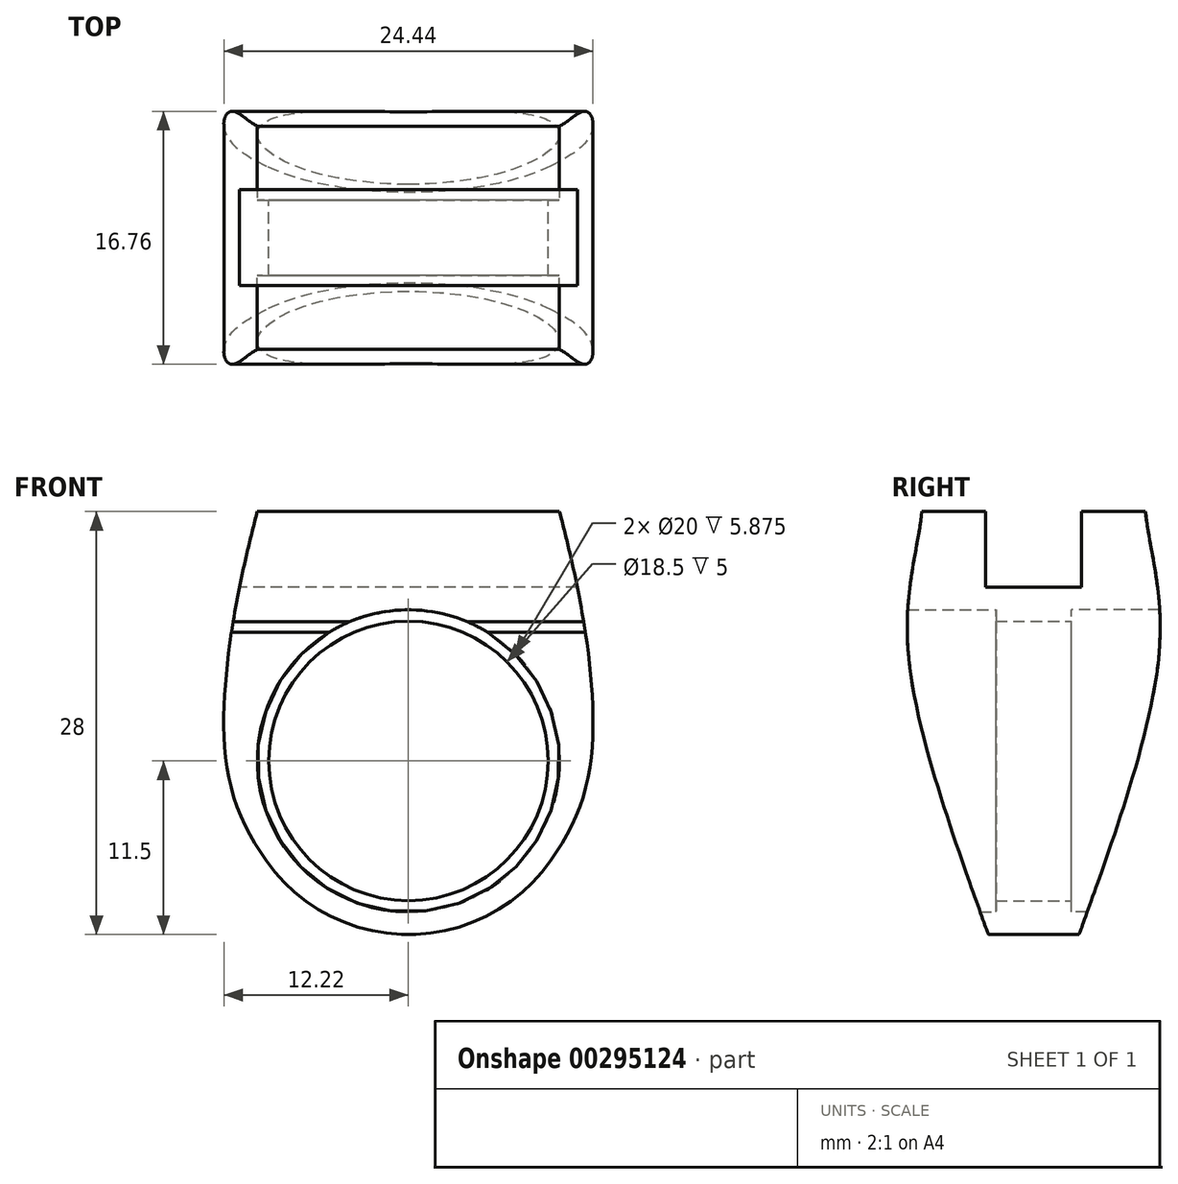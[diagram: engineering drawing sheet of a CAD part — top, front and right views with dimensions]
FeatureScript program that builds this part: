
annotation { "Feature Type Name" : "Feature", "Feature Type Description" : "" }
export const myFeature = defineFeature(function(context is Context, id is Id, definition is map)
    precondition{}
    {
        {
            var Q0;
            Q0=qCreatedBy(makeId("Front.planeOp"),FACE);
            var sketch = newSketch(context, id + "F0", { "sketchPlane" : qUnion([Q0])});
            skCircle(sketch, "E0", {"center": v(0, 0) * mm, "radius": 8.5 * mm});
            skCircle(sketch, "E1", {"center": v(0, 0) * mm, "radius": 11.5 * mm});
            skSolve(sketch);
        }
        {
            var Q0;
            Q0=qCreatedBy(makeId("Front.planeOp"),FACE);
            var sketch = newSketch(context, id + "F1", { "sketchPlane" : qUnion([Q0])});
            skLineSegment(sketch, "E2", {"start": v(-10, 16.5) * mm, "end": v(10, 16.5) * mm});
            skLineSegment(sketch, "E3", {"start": v(-8.5, 0) * mm, "end": v(-11.5, 0) * mm, "construction": true});
            skLineSegment(sketch, "E4", {"start": v(-10, 16.5) * mm, "end": v(-10, 0) * mm, "construction": true});
            skLineSegment(sketch, "E5", {"start": v(-10, 16.5) * mm, "end": v(-14.42, 0) * mm, "construction": true});
            skLineSegment(sketch, "E6", {"start": v(0, 0) * mm, "end": v(-9.42, -6.6) * mm, "construction": true});
            skFitSpline(sketch, "E7", {"points": [v(-9.42, -6.6) * mm, v(-12.07, 0) * mm, v(-10, 16.5) * mm], "startDerivative": vector(-9.97, 14.24) * mm, "endDerivative": vector(8.14, 30.38) * mm});
            skLineSegment(sketch, "E8", {"start": v(-9.42, -6.6) * mm, "end": v(-7.7, -9.05) * mm, "construction": true});
            skFitSpline(sketch, "E9.MirrorCS", {"points": [v(9.42, -6.6) * mm, v(12.07, 0) * mm, v(10, 16.5) * mm], "startDerivative": vector(9.97, 14.24) * mm, "endDerivative": vector(-8.14, 30.38) * mm});
            skCircle(sketch, "E10", {"center": v(0, 0) * mm, "radius": 8.5 * mm});
            skArc(sketch, "E11", {"start": v(-9.42, -6.6) * mm, "mid": v(0, -11.5) * mm, "end": v(9.42, -6.6) * mm});
            skSolve(sketch);
        }
        {
            var Q0;
            Q0 = qSketchRegion(id + "F1", true);
            extrude(context, id + "F2", {"entities" : qUnion([Q0]), "endBound" : BoundingType.SYMMETRIC, "depth" : 16.75 * mm});
        }
        {
            var Q0;
            Q0=qCreatedBy(makeId("Right.planeOp"),FACE);
            var sketch = newSketch(context, id + "F3", { "sketchPlane" : qUnion([Q0])});
            skLineSegment(sketch, "E12", {"start": v(0, 8.5) * mm, "end": v(-8.38, 8.5) * mm, "construction": true});
            skLineSegment(sketch, "E13", {"start": v(0, -11.5) * mm, "end": v(-3, -11.5) * mm});
            skLineSegment(sketch, "E14", {"start": v(-3, -11.5) * mm, "end": v(-8.38, -11.5) * mm, "construction": true});
            skLineSegment(sketch, "E15", {"start": v(-8.38, 8.5) * mm, "end": v(-7.4, 16.5) * mm, "construction": true});
            skLineSegment(sketch, "E16", {"start": v(-7.4, 16.5) * mm, "end": v(0, 16.5) * mm, "construction": true});
            skLineSegment(sketch, "E17", {"start": v(-7.4, 16.5) * mm, "end": v(-8.38, 16.5) * mm, "construction": true});
            skFitSpline(sketch, "E18", {"points": [v(-7.4, 16.5) * mm, v(-8.38, 8.5) * mm, v(-3, -11.5) * mm], "startDerivative": vector(-2.37, -19.33) * mm, "endDerivative": vector(15.27, -41.97) * mm});
            skLineSegment(sketch, "E19", {"start": v(-3, -11.5) * mm, "end": v(0, -19.74) * mm});
            skLineSegment(sketch, "E20", {"start": v(-7.4, 16.5) * mm, "end": v(0, 23.23) * mm});
            skLineSegment(sketch, "E21.MirrorCS", {"start": v(7.4, 16.5) * mm, "end": v(0, 23.23) * mm});
            skFitSpline(sketch, "E22.MirrorCS", {"points": [v(7.4, 16.5) * mm, v(8.38, 8.5) * mm, v(3, -11.5) * mm], "startDerivative": vector(2.37, -19.33) * mm, "endDerivative": vector(-15.27, -41.97) * mm});
            skLineSegment(sketch, "E23.MirrorCS", {"start": v(3, -11.5) * mm, "end": v(0, -19.74) * mm});
            skSolve(sketch);
        }
        {
            var Q0;
            Q0 = qSketchRegion(id + "F3", true);
            extrude(context, id + "F4", {"entities" : qUnion([Q0]), "operationType" : NewBodyOperationType.INTERSECT, "endBound" : BoundingType.SYMMETRIC, "depth" : 50 * mm});
        }
        {
            var Q0;
            Q0=qCreatedBy(makeId("Front.planeOp"),FACE);
            var sketch = newSketch(context, id + "F5", { "sketchPlane" : qUnion([Q0])});
            skCircle(sketch, "E24", {"center": v(0, 0) * mm, "radius": 9.25 * mm});
            skSolve(sketch);
        }
        {
            var Q0;
            Q0 = qSketchRegion(id + "F5", true);
            extrude(context, id + "F6", {"entities" : qUnion([Q0]), "operationType" : NewBodyOperationType.REMOVE, "endBound" : BoundingType.SYMMETRIC, "depth" : 50 * mm});
        }
        {
            var Q0;
            Q0=qCreatedBy(makeId("Front.planeOp"),FACE);
            cPlane(context, id + "F7", {"entities" : qUnion([Q0]), "cplaneType" : CPlaneType.OFFSET, "offset" : 2.5 * mm, "width" : 150 * mm, "height" : 150 * mm});
        }
        {
            var Q0;
            Q0=qCreatedBy(id+"F7.planeOp",FACE);
            var sketch = newSketch(context, id + "F8", { "sketchPlane" : qUnion([Q0])});
            skCircle(sketch, "E25", {"center": v(0, 0) * mm, "radius": 10 * mm});
            skSolve(sketch);
        }
        {
            var Q0;
            Q0 = qSketchRegion(id + "F8", true);
            extrude(context, id + "F9", {"entities" : qUnion([Q0]), "operationType" : NewBodyOperationType.REMOVE, "depth" : 25 * mm});
        }
        {
            var Q0;
            Q0=qCreatedBy(makeId("Front.planeOp"),FACE);
            cPlane(context, id + "F10", {"entities" : qUnion([Q0]), "cplaneType" : CPlaneType.OFFSET, "offset" : 2.5 * mm, "oppositeDirection" : true, "width" : 150 * mm, "height" : 150 * mm});
        }
        {
            var Q0;
            Q0=qCreatedBy(id+"F10.planeOp",FACE);
            var sketch = newSketch(context, id + "F11", { "sketchPlane" : qUnion([Q0])});
            skCircle(sketch, "E26", {"center": v(0, 0) * mm, "radius": 10 * mm});
            skSolve(sketch);
        }
        {
            var Q0;
            Q0 = qSketchRegion(id + "F11", true);
            extrude(context, id + "F12", {"entities" : qUnion([Q0]), "operationType" : NewBodyOperationType.REMOVE, "oppositeDirection" : true, "depth" : 25 * mm});
        }
        {
            var Q0;
            Q0=makeQuery(id+"F2.opExtrude","SWEPT_FACE",FACE,{"disambiguationData":[OSD([sQuery(id+"F1.wireOp",EDGE,"E2")])]});
            cPlane(context, id + "F13", {"entities" : qUnion([Q0]), "cplaneType" : CPlaneType.OFFSET, "offset" : 5 * mm, "oppositeDirection" : true, "width" : 150 * mm, "height" : 150 * mm});
        }
        {
            var Q0;
            Q0=qCreatedBy(makeId("Right.planeOp"),FACE);
            var sketch = newSketch(context, id + "F14", { "sketchPlane" : qUnion([Q0])});
            skLineSegment(sketch, "E27.bottom", {"start": v(3.18, 11.5) * mm, "end": v(-3.18, 11.5) * mm});
            skLineSegment(sketch, "E27.top", {"start": v(3.17, 26.5) * mm, "end": v(-3.17, 26.5) * mm});
            skLineSegment(sketch, "E27.left", {"start": v(3.17, 11.5) * mm, "end": v(3.18, 26.5) * mm});
            skLineSegment(sketch, "E27.right", {"start": v(-3.18, 11.5) * mm, "end": v(-3.17, 26.5) * mm});
            skSolve(sketch);
        }
        {
            var Q0;
            Q0=makeQuery(id+"F14.imprint","IMPRINT",FACE,{"disambiguationData":[TD([[makeQuery(id+"F14.imprint","IMPRINT",EDGE,{"derivedFrom":sQuery(id+"F14.wireOp",EDGE,"E27.bottom")}),-1.0]])]});
            extrude(context, id + "F15", {"entities" : qUnion([Q0]), "operationType" : NewBodyOperationType.REMOVE, "endBound" : BoundingType.SYMMETRIC, "depth" : 50 * mm});
        }
    });
